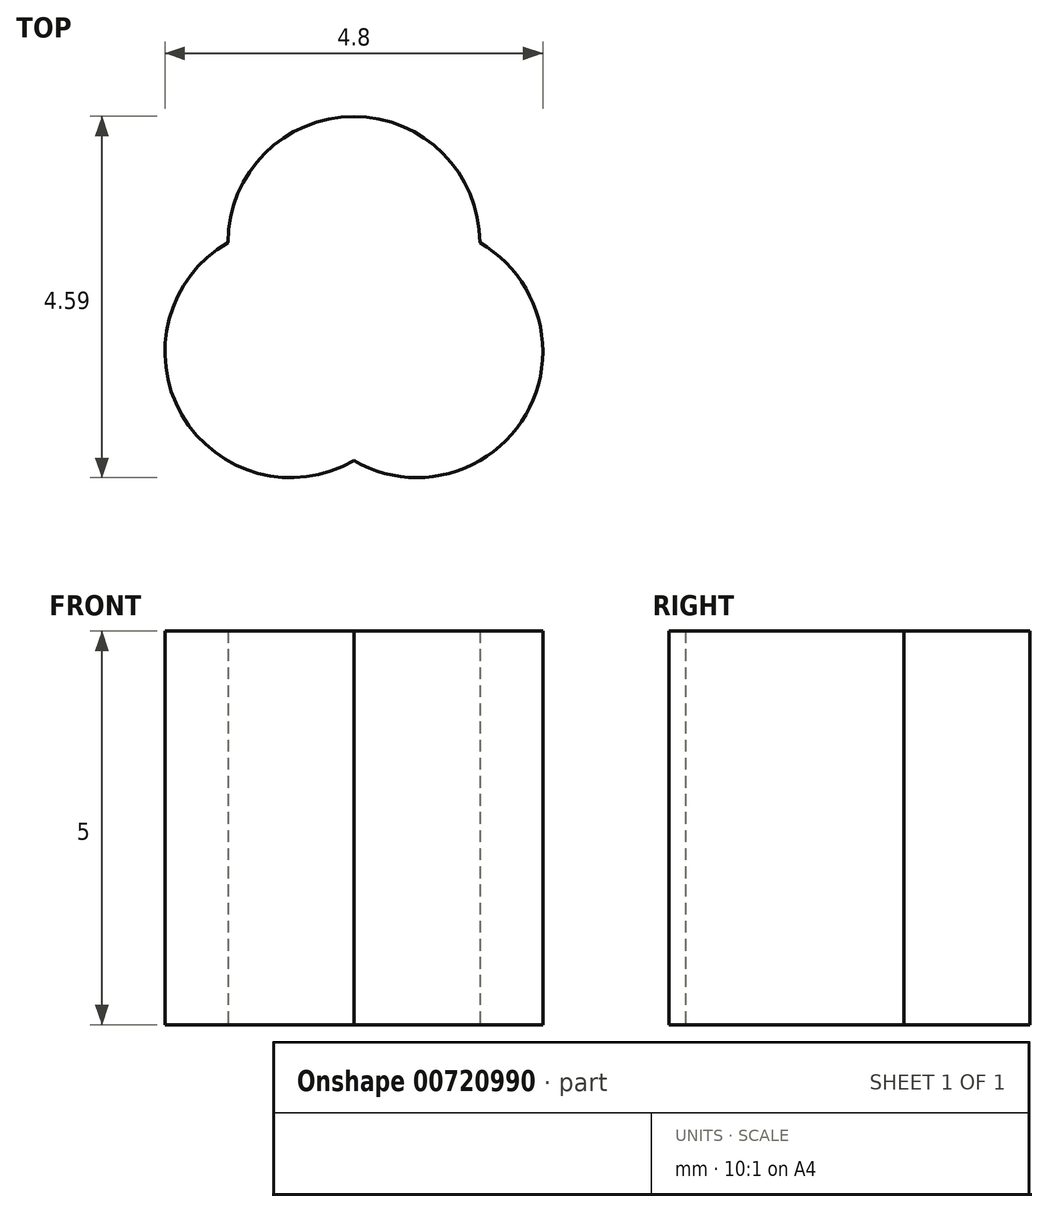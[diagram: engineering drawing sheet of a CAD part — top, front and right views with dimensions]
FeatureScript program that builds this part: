
annotation { "Feature Type Name" : "Feature", "Feature Type Description" : "" }
export const myFeature = defineFeature(function(context is Context, id is Id, definition is map)
    precondition{}
    {
        {
            var Q0;
            Q0=qCreatedBy(makeId("Top.planeOp"),FACE);
            var sketch = newSketch(context, id + "F0", { "sketchPlane" : qUnion([Q0])});
            skCircle(sketch, "E0", {"center": v(0, 0) * mm, "radius": 1.6 * mm});
            skCircle(sketch, "E1", {"center": v(-1.6, 0) * mm, "radius": 1.6 * mm});
            skCircle(sketch, "E2", {"center": v(-0.8, 1.39) * mm, "radius": 1.6 * mm});
            skSolve(sketch);
        }
        {
            var Q0;
            {var subQ0=sQuery(id+"F0.wireOp",EDGE,"E1");var subQ1=sQuery(id+"F0.wireOp",EDGE,"E0");var subQ2=makeQuery(id+"F0.imprint","INTERSECT",VERTEX,{"disambiguationData":[OD(0.0)],"derivedFrom":[subQ1,subQ0]});Q0=makeQuery(id+"F0.imprint","IMPRINT",FACE,{"disambiguationData":[TD([[makeQuery(id+"F0.imprint","IMPRINT",EDGE,{"disambiguationData":[TD([[subQ2,1.0]])],"derivedFrom":subQ1}),-1.0]])]});}
            var Q1;
            {var subQ0=sQuery(id+"F0.wireOp",EDGE,"E2");var subQ1=sQuery(id+"F0.wireOp",EDGE,"E0");var subQ2=makeQuery(id+"F0.imprint","INTERSECT",VERTEX,{"disambiguationData":[OD(0.0)],"derivedFrom":[subQ1,subQ0]});Q1=makeQuery(id+"F0.imprint","IMPRINT",FACE,{"disambiguationData":[TD([[makeQuery(id+"F0.imprint","IMPRINT",EDGE,{"disambiguationData":[TD([[subQ2,1.0]])],"derivedFrom":subQ1}),1.0]])]});}
            var Q2;
            {var subQ0=sQuery(id+"F0.wireOp",EDGE,"E2");var subQ1=sQuery(id+"F0.wireOp",EDGE,"E0");var subQ2=makeQuery(id+"F0.imprint","INTERSECT",VERTEX,{"disambiguationData":[OD(0.0)],"derivedFrom":[subQ1,subQ0]});Q2=makeQuery(id+"F0.imprint","IMPRINT",FACE,{"disambiguationData":[TD([[makeQuery(id+"F0.imprint","IMPRINT",EDGE,{"disambiguationData":[TD([[subQ2,-1.0]])],"derivedFrom":subQ1}),1.0]])]});}
            var Q3;
            {var subQ0=sQuery(id+"F0.wireOp",EDGE,"E2");var subQ1=sQuery(id+"F0.wireOp",EDGE,"E0");var subQ2=makeQuery(id+"F0.imprint","INTERSECT",VERTEX,{"disambiguationData":[OD(0.0)],"derivedFrom":[subQ1,subQ0]});Q3=makeQuery(id+"F0.imprint","IMPRINT",FACE,{"disambiguationData":[TD([[makeQuery(id+"F0.imprint","IMPRINT",EDGE,{"disambiguationData":[TD([[subQ2,-1.0]])],"derivedFrom":subQ1}),-1.0]])]});}
            var Q4;
            {var subQ0=sQuery(id+"F0.wireOp",EDGE,"E1");var subQ1=sQuery(id+"F0.wireOp",EDGE,"E0");var subQ2=makeQuery(id+"F0.imprint","INTERSECT",VERTEX,{"disambiguationData":[OD(1.0)],"derivedFrom":[subQ1,subQ0]});Q4=makeQuery(id+"F0.imprint","IMPRINT",FACE,{"disambiguationData":[TD([[makeQuery(id+"F0.imprint","IMPRINT",EDGE,{"disambiguationData":[TD([[subQ2,-1.0]])],"derivedFrom":subQ1}),-1.0]])]});}
            var Q5;
            {var subQ0=sQuery(id+"F0.wireOp",EDGE,"E1");var subQ1=sQuery(id+"F0.wireOp",EDGE,"E0");var subQ2=makeQuery(id+"F0.imprint","INTERSECT",VERTEX,{"disambiguationData":[OD(0.0)],"derivedFrom":[subQ1,subQ0]});Q5=makeQuery(id+"F0.imprint","IMPRINT",FACE,{"disambiguationData":[TD([[makeQuery(id+"F0.imprint","IMPRINT",EDGE,{"disambiguationData":[TD([[subQ2,1.0]])],"derivedFrom":subQ1}),1.0]])]});}
            var Q6;
            {var subQ0=sQuery(id+"F0.wireOp",EDGE,"E1");var subQ1=sQuery(id+"F0.wireOp",EDGE,"E0");var subQ2=makeQuery(id+"F0.imprint","INTERSECT",VERTEX,{"disambiguationData":[OD(1.0)],"derivedFrom":[subQ1,subQ0]});Q6=makeQuery(id+"F0.imprint","IMPRINT",FACE,{"disambiguationData":[TD([[makeQuery(id+"F0.imprint","IMPRINT",EDGE,{"disambiguationData":[TD([[subQ2,-1.0]])],"derivedFrom":subQ1}),1.0]])]});}
            extrude(context, id + "F1", {"entities" : qUnion([Q0, Q1, Q2, Q3, Q4, Q5, Q6]), "depth" : 5 * mm, "offsetDistance" : 25 * mm});
        }
    });
